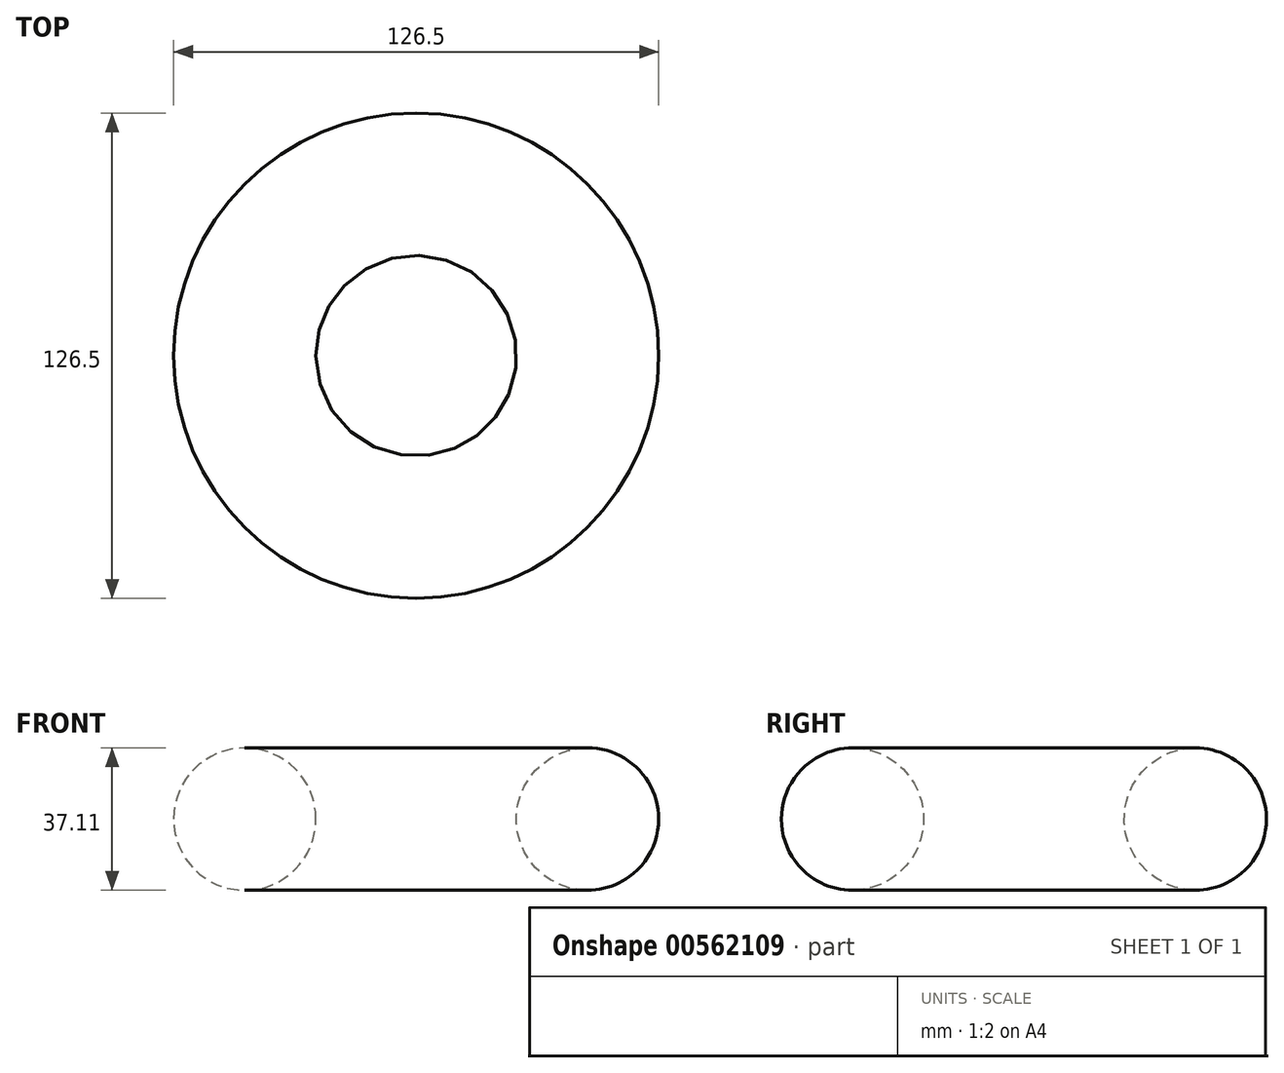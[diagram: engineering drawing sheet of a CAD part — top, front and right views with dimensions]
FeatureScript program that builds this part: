
annotation { "Feature Type Name" : "Feature", "Feature Type Description" : "" }
export const myFeature = defineFeature(function(context is Context, id is Id, definition is map)
    precondition{}
    {
        {
            var Q0;
            Q0=qCreatedBy(makeId("Front.planeOp"),FACE);
            var sketch = newSketch(context, id + "F0", { "sketchPlane" : qUnion([Q0])});
            skCircle(sketch, "E0", {"center": v(44.7, 25) * mm, "radius": 18.55 * mm});
            skLineSegment(sketch, "E1", {"start": v(0, 0) * mm, "end": v(0, 51.88) * mm, "construction": true});
            skSolve(sketch);
        }
        {
            var Q0;
            Q0=makeQuery(id+"F0.imprint","IMPRINT",FACE,{"disambiguationData":[TD([[makeQuery(id+"F0.imprint","IMPRINT",EDGE,{"derivedFrom":sQuery(id+"F0.wireOp",EDGE,"E0")}),1.0]])]});
            var Q1;
            Q1=sQuery(id+"F0.wireOp",EDGE,"E1");
            revolve(context, id + "F1", {"entities" : qUnion([Q0]), "axis" : qUnion([Q1]), "revolveType" : RevolveType.FULL});
        }
    });
